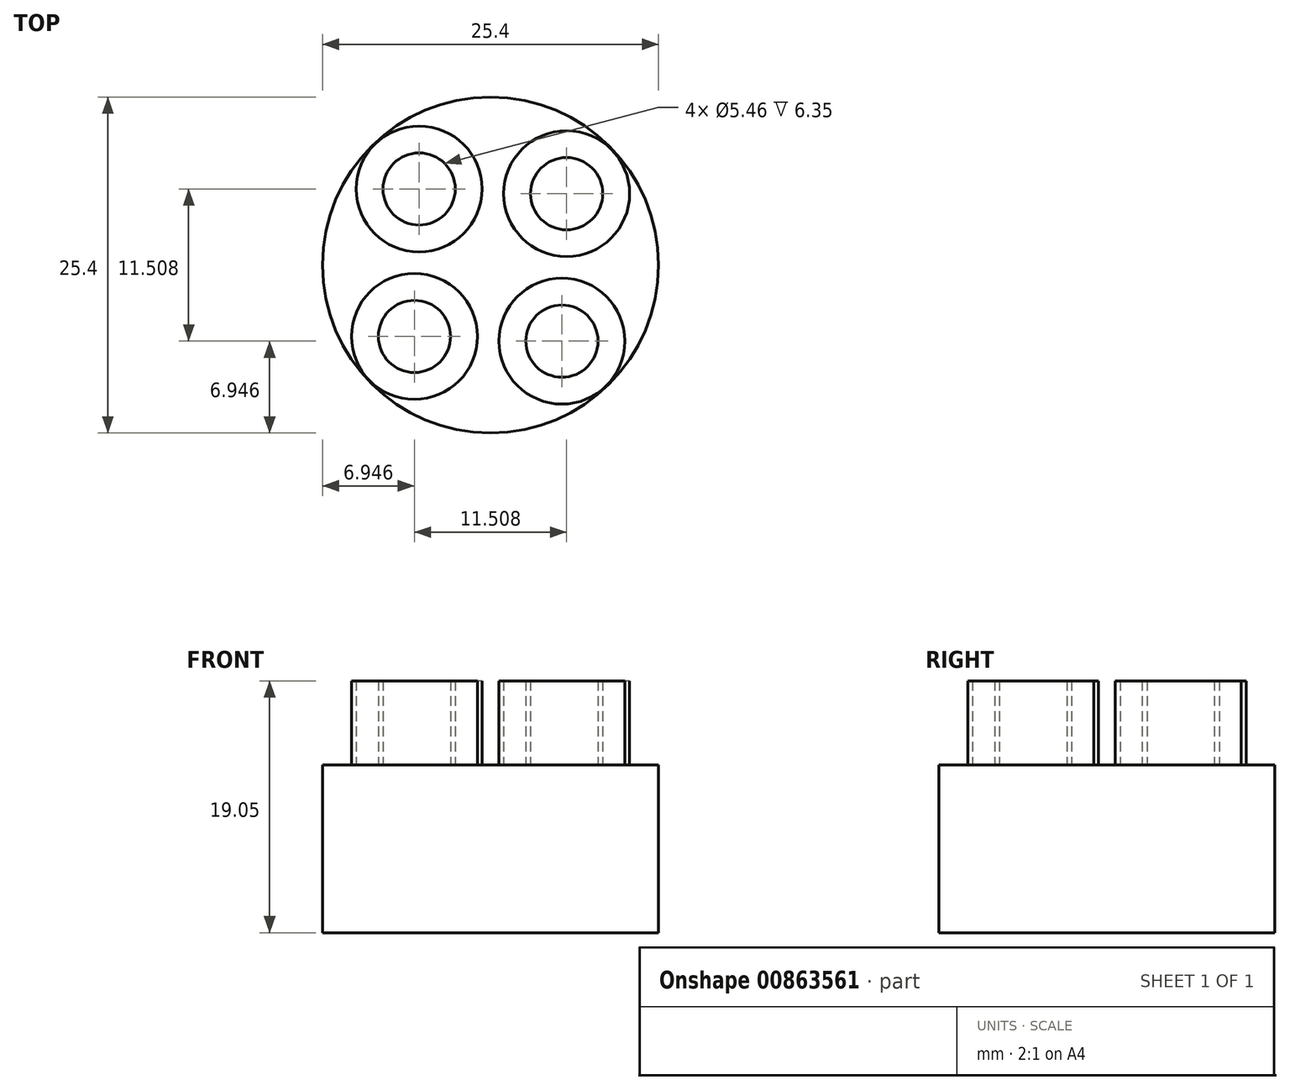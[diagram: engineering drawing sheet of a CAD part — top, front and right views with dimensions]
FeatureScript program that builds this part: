
annotation { "Feature Type Name" : "Feature", "Feature Type Description" : "" }
export const myFeature = defineFeature(function(context is Context, id is Id, definition is map)
    precondition{}
    {
        {
            var Q0;
            Q0=qCreatedBy(makeId("Top.planeOp"),FACE);
            var sketch = newSketch(context, id + "F0", { "sketchPlane" : qUnion([Q0])});
            skCircle(sketch, "E0", {"center": v(0, 0) * mm, "radius": 12.7 * mm});
            skSolve(sketch);
        }
        {
            var Q0;
            Q0=makeQuery(id+"F0.imprint","IMPRINT",FACE,{"disambiguationData":[TD([[makeQuery(id+"F0.imprint","IMPRINT",EDGE,{"derivedFrom":sQuery(id+"F0.wireOp",EDGE,"E0")}),1.0]])]});
            extrude(context, id + "F1", {"entities" : qUnion([Q0]), "depth" : 12.7 * mm, "offsetDistance" : 25.4 * mm});
        }
        {
            var Q0;
            Q0=qCreatedBy(makeId("Top.planeOp"),FACE);
            cPlane(context, id + "F2", {"entities" : qUnion([Q0]), "cplaneType" : CPlaneType.OFFSET, "offset" : 12.7 * mm, "width" : 152.4 * mm, "height" : 152.4 * mm});
        }
        {
            var Q0;
            Q0=qCreatedBy(id+"F2.planeOp",FACE);
            var sketch = newSketch(context, id + "F3", { "sketchPlane" : qUnion([Q0])});
            skCircle(sketch, "E1", {"center": v(-5.4, 5.75) * mm, "radius": 4.76 * mm});
            skCircle(sketch, "E2.0", {"center": v(-5.4, 5.75) * mm, "radius": 2.73 * mm});
            skCircle(sketch, "E3.1.0", {"center": v(-5.75, -5.4) * mm, "radius": 4.76 * mm});
            skCircle(sketch, "E3.1.1", {"center": v(-5.75, -5.4) * mm, "radius": 2.73 * mm});
            skCircle(sketch, "E3.2.0", {"center": v(5.4, -5.75) * mm, "radius": 4.76 * mm});
            skCircle(sketch, "E3.2.1", {"center": v(5.4, -5.75) * mm, "radius": 2.73 * mm});
            skCircle(sketch, "E3.3.0", {"center": v(5.75, 5.4) * mm, "radius": 4.76 * mm});
            skCircle(sketch, "E3.3.1", {"center": v(5.75, 5.4) * mm, "radius": 2.73 * mm});
            skPoint(sketch, "E3.center", {"position": v(0, 0) * mm});
            skSolve(sketch);
        }
        {
            var Q0;
            Q0 = qSketchRegion(id + "F3", true);
            extrude(context, id + "F4", {"entities" : qUnion([Q0]), "operationType" : NewBodyOperationType.ADD, "depth" : 6.35 * mm, "offsetDistance" : 25.4 * mm});
        }
    });
